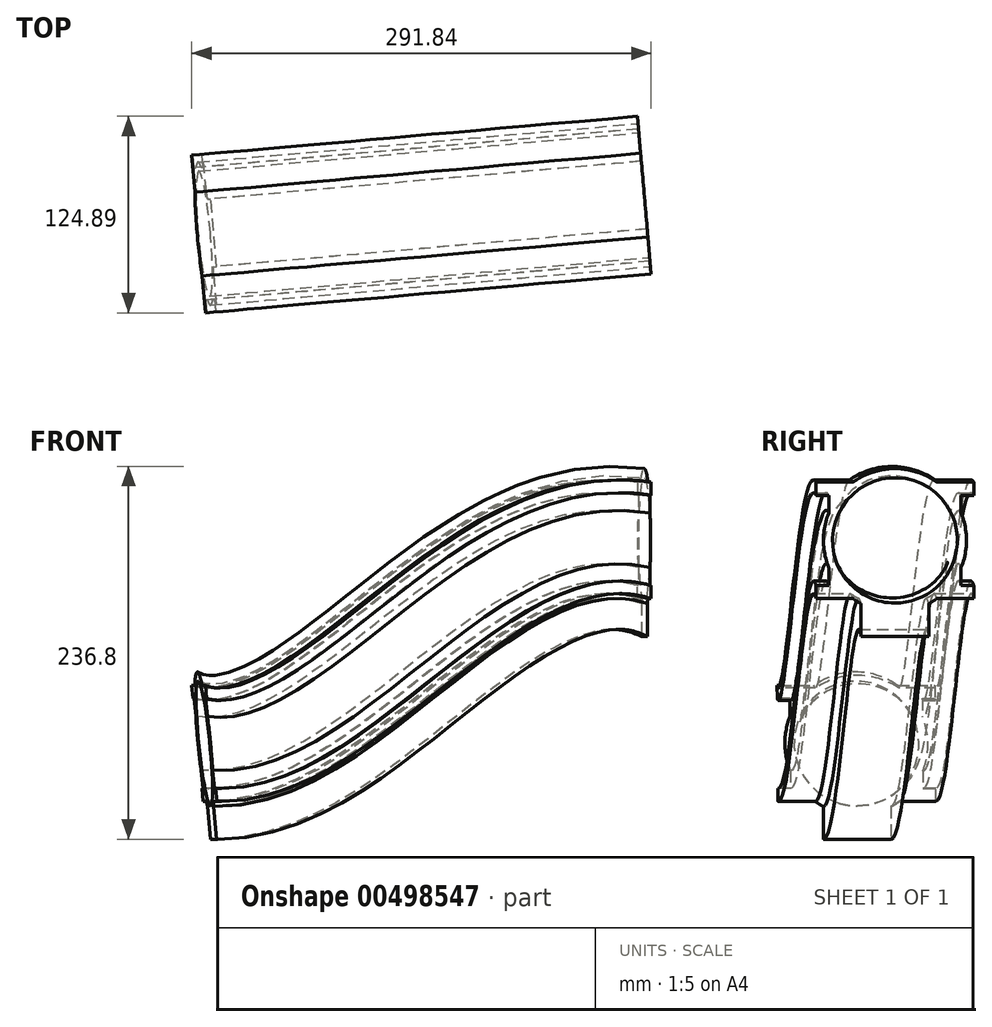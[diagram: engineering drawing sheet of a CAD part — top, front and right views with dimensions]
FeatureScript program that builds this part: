
annotation { "Feature Type Name" : "Feature", "Feature Type Description" : "" }
export const myFeature = defineFeature(function(context is Context, id is Id, definition is map)
    precondition{}
    {
        {
            var Q0;
            Q0=qCreatedBy(makeId("Front.planeOp"),FACE);
            var sketch = newSketch(context, id + "F0", { "sketchPlane" : qUnion([Q0])});
            skCircle(sketch, "E0", {"center": v(0, 0) * mm, "radius": 39.8 * mm});
            skLineSegment(sketch, "E1.bottom", {"start": v(-42.18, 36.97) * mm, "end": v(-26.7, 36.97) * mm});
            skLineSegment(sketch, "E1.top", {"start": v(-42.18, -36.97) * mm, "end": v(-26.7, -36.97) * mm});
            skLineSegment(sketch, "E1.left", {"start": v(-42.18, 28.68) * mm, "end": v(-42.18, 17.32) * mm});
            skLineSegment(sketch, "E1.right", {"start": v(42.18, 28.68) * mm, "end": v(42.18, 17.32) * mm});
            skLineSegment(sketch, "E2", {"start": v(21.56, -40.18) * mm, "end": v(21.56, -61.1) * mm});
            skLineSegment(sketch, "E3", {"start": v(21.56, -61.1) * mm, "end": v(0, -61.1) * mm});
            skLineSegment(sketch, "E4", {"start": v(0, -11.75) * mm, "end": v(0, -25.23) * mm, "construction": true});
            skLineSegment(sketch, "E5.bottom", {"start": v(42.18, 36.97) * mm, "end": v(50.25, 36.97) * mm});
            skLineSegment(sketch, "E5.top", {"start": v(42.18, 28.68) * mm, "end": v(50.25, 28.68) * mm});
            skLineSegment(sketch, "E5.right", {"start": v(50.25, 36.97) * mm, "end": v(50.25, 28.68) * mm});
            skLineSegment(sketch, "E6.MirrorCS", {"start": v(-42.18, 36.97) * mm, "end": v(-50.25, 36.97) * mm});
            skLineSegment(sketch, "E7.MirrorCS", {"start": v(-50.25, 36.97) * mm, "end": v(-50.25, 28.68) * mm});
            skLineSegment(sketch, "E8.MirrorCS", {"start": v(-42.18, 28.68) * mm, "end": v(-50.25, 28.68) * mm});
            skLineSegment(sketch, "E9.MirrorCS", {"start": v(-21.56, -40.18) * mm, "end": v(-21.56, -61.1) * mm});
            skLineSegment(sketch, "E10.MirrorCS", {"start": v(-21.56, -61.1) * mm, "end": v(0, -61.1) * mm});
            skLineSegment(sketch, "E11.trimOffspring", {"start": v(26.7, 36.97) * mm, "end": v(42.18, 36.97) * mm});
            skLineSegment(sketch, "E12.trimOffspring", {"start": v(26.7, -36.97) * mm, "end": v(42.18, -36.97) * mm});
            skLineSegment(sketch, "E13.MirrorCS", {"start": v(-42.18, -36.97) * mm, "end": v(-50.25, -36.97) * mm});
            skLineSegment(sketch, "E14.MirrorCS", {"start": v(-42.18, -28.68) * mm, "end": v(-50.25, -28.68) * mm});
            skLineSegment(sketch, "E15.MirrorCS", {"start": v(-50.25, -36.97) * mm, "end": v(-50.25, -28.68) * mm});
            skLineSegment(sketch, "E16.MirrorCS", {"start": v(42.18, -36.97) * mm, "end": v(50.25, -36.97) * mm});
            skLineSegment(sketch, "E17.MirrorCS", {"start": v(50.25, -36.97) * mm, "end": v(50.25, -28.68) * mm});
            skLineSegment(sketch, "E18.MirrorCS", {"start": v(42.18, -28.68) * mm, "end": v(50.25, -28.68) * mm});
            skArc(sketch, "E19.0", {"start": v(26.7, 36.97) * mm, "mid": v(0, 45.6) * mm, "end": v(-26.7, 36.97) * mm});
            skLineSegment(sketch, "E20.trimOffspring", {"start": v(42.18, -17.32) * mm, "end": v(42.18, -28.68) * mm});
            skArc(sketch, "E21.trimOffspring", {"start": v(42.18, -17.32) * mm, "mid": v(45.6, 0) * mm, "end": v(42.18, 17.32) * mm});
            skPoint(sketch, "E22.orphan", {"position": v(21.56, -36.97) * mm});
            skPoint(sketch, "E23.orphan", {"position": v(-21.56, -36.97) * mm});
            skArc(sketch, "E24.trimOffspring", {"start": v(-26.7, -36.97) * mm, "mid": v(-24.18, -38.66) * mm, "end": v(-21.56, -40.18) * mm});
            skArc(sketch, "E25.trimOffspring", {"start": v(21.56, -40.18) * mm, "mid": v(24.18, -38.66) * mm, "end": v(26.7, -36.97) * mm});
            skLineSegment(sketch, "E26.trimOffspring", {"start": v(-42.18, -17.32) * mm, "end": v(-42.18, -28.68) * mm});
            skArc(sketch, "E27.trimOffspring", {"start": v(-42.18, 17.32) * mm, "mid": v(-45.6, 0) * mm, "end": v(-42.18, -17.32) * mm});
            skSolve(sketch);
        }
        {
            var Q0;
            Q0=qCreatedBy(makeId("Right.planeOp"),FACE);
            var sketch = newSketch(context, id + "F1", { "sketchPlane" : qUnion([Q0])});
            skFitSpline(sketch, "E28", {"points": [v(0, 0) * mm, v(280.52, -129) * mm], "startDerivative": vector(319.98, 64.77) * mm, "endDerivative": vector(253.82, 25.7) * mm});
            skSolve(sketch);
        }
        {
            var Q0;
            Q0=makeQuery(id+"F0.imprint","IMPRINT",FACE,{"disambiguationData":[TD([[makeQuery(id+"F0.imprint","IMPRINT",EDGE,{"derivedFrom":sQuery(id+"F0.wireOp",EDGE,"E0")}),-1.0]])]});
            var Q1;
            Q1=sQuery(id+"F1.wireOp",EDGE,"E28");
            sweep(context, id + "F2", {"profiles" : qUnion([Q0]), "path" : qUnion([Q1])});
        }
        {
            var Q0;
            Q0=qCreatedBy(makeId("Right.planeOp"),FACE);
            var sketch = newSketch(context, id + "F3", { "sketchPlane" : qUnion([Q0])});
            skLineSegment(sketch, "E29", {"start": v(0, 0) * mm, "end": v(0, 92.68) * mm, "construction": true});
            skSolve(sketch);
        }
        {
            var Q0;
            Q0=makeQuery(id+"F2.opSweep","SWEPT_BODY",BODY,{"disambiguationData":[OSD([sQuery(id+"F0.wireOp",EDGE,"E0"),sQuery(id+"F0.wireOp",EDGE,"E1.bottom"),sQuery(id+"F0.wireOp",EDGE,"E1.top"),sQuery(id+"F0.wireOp",EDGE,"E1.left"),sQuery(id+"F0.wireOp",EDGE,"E1.right"),sQuery(id+"F0.wireOp",EDGE,"E2"),sQuery(id+"F0.wireOp",EDGE,"E3"),sQuery(id+"F0.wireOp",EDGE,"E5.bottom"),sQuery(id+"F0.wireOp",EDGE,"E5.top"),sQuery(id+"F0.wireOp",EDGE,"E5.right"),sQuery(id+"F0.wireOp",EDGE,"E6.MirrorCS"),sQuery(id+"F0.wireOp",EDGE,"E7.MirrorCS"),sQuery(id+"F0.wireOp",EDGE,"E8.MirrorCS"),sQuery(id+"F0.wireOp",EDGE,"E9.MirrorCS"),sQuery(id+"F0.wireOp",EDGE,"E10.MirrorCS"),sQuery(id+"F0.wireOp",EDGE,"E11.trimOffspring"),sQuery(id+"F0.wireOp",EDGE,"E12.trimOffspring"),sQuery(id+"F0.wireOp",EDGE,"E13.MirrorCS"),sQuery(id+"F0.wireOp",EDGE,"E14.MirrorCS"),sQuery(id+"F0.wireOp",EDGE,"E15.MirrorCS"),sQuery(id+"F0.wireOp",EDGE,"E16.MirrorCS"),sQuery(id+"F0.wireOp",EDGE,"E17.MirrorCS"),sQuery(id+"F0.wireOp",EDGE,"E18.MirrorCS"),sQuery(id+"F0.wireOp",EDGE,"E19.0"),sQuery(id+"F0.wireOp",EDGE,"E20.trimOffspring"),sQuery(id+"F0.wireOp",EDGE,"E21.trimOffspring"),sQuery(id+"F0.wireOp",EDGE,"E24.trimOffspring"),sQuery(id+"F0.wireOp",EDGE,"E25.trimOffspring"),sQuery(id+"F0.wireOp",EDGE,"E26.trimOffspring"),sQuery(id+"F0.wireOp",EDGE,"E27.trimOffspring"),sQuery(id+"F1.wireOp",EDGE,"E28")])]});
            var Q1;
            Q1=sQuery(id+"F3.wireOp",EDGE,"E29");
            transform(context, id + "F4", {"entities" : qUnion([Q0]), "transformType" : TransformType.ROTATION, "transformAxis" : qUnion([Q1]), "angle" : 95 * degree, "makeCopy" : false});
        }
    });
